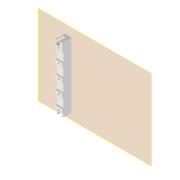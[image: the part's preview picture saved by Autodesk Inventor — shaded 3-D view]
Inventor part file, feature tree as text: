
AUTODESK INVENTOR PART (.ipt)
format: ipt  version: 2022 (Build 260153000, 153)  size: 180,736 bytes
history: native  units: mm
features: reference x9, other x6, projected_geometry x5, sketch x4, extrude x3, plane x2, pattern_linear x1, hole x1
ambient origin geometry x8: Origin, YZ Plane, XZ Plane, XY Plane, X Axis, Y Axis, Z Axis, Center Point
bodies: Volumenkörper1 (feature_tree)
feature tree (31):
  plane  "Arbeitsebene1"
  sketch  "Skizze1"  dims[d0=3.0mm d1=3.0mm]
  plane  "Arbeitsebene2"
  extrude  "Extrusion1"  Depth=3.0mm
  extrude  "Extrusion2"  Depth=6.0mm
  pattern_linear  "Rechteckige Anordnung1"  Spacing1=10.0mm  [1 undecoded]
  extrude  "Extrusion3"  Depth=9.0mm
  hole  "Bohrung1"  [1 undecoded]
  reference  "Referenz1"
  sketch  "Skizze2"  dims[d2=3.0mm d3=6.0mm]
  reference  "Referenz2"
  reference  "Referenz3"
  reference  "Referenz4"
  reference  "Referenz5"
  reference  "Referenz6"
  reference  "Referenz7"
  reference  "Referenz8"
  reference  "Referenz9"
  sketch  "Skizze3"  dims[d4=2.8mm]
  projected_geometry  "Projizierte Kontur1"
  projected_geometry  "Projizierte Kontur2"
  projected_geometry  "Projizierte Kontur3"
  sketch  "Skizze4"  dims[d5=2.8mm d6=10.0mm d7=0.0mm d8=0.2mm d9=2.0mm d10=0.0mm d11=50.0mm d13=18.7mm d14=2.8mm d15=2.8mm d16=2.8mm d17=0.0mm d18=0.0mm d19=3.2mm d20=6.0mm d21=7.0mm d22=9.0mm d23=90.0deg d24=8.0mm d25=20.594885mm]
  projected_geometry  "Projizierte Kontur4"
  projected_geometry  "Projizierte Kontur5"
  other  "Baugruppe1"
  other  "Omniscope_USBC_Base_Top+:1"
  other  "00_Seeeduino Xiao:19"
  other  "00_Seeeduino Xiao:13"
  other  "00_Seeeduino Xiao:7"
  other  "00_Seeeduino Xiao:1"
note: 2 required parameter values undecoded (feature->parameter linkage not recoverable at this tier; creation-order binding heuristic only, values carry confidence <= 0.55)
